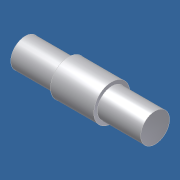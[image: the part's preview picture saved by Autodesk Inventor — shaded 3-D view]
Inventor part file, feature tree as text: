
AUTODESK INVENTOR PART (.ipt)
format: ipt  version: unknown  size: 171,520 bytes
history: native  units: in
note: dims shown in document units (in); Inventor stores cm internally (conversion verified against a paired STEP export)
features: revolve x1, sketch x1
ambient origin geometry x8: Origin, YZ Plane, XZ Plane, XY Plane, X Axis, Y Axis, Z Axis, Center Point
bodies: Solid1 (feature_tree)
feature tree (2):
  revolve  "Revolution1"  [1 undecoded]
  sketch  "Sketch1"  dims[d0=0.375in d1=0.375in d2=0.375in d3=0.125in d4=0.125in d5=0.1562in d6=90.0deg]
note: 1 required parameter value undecoded (feature->parameter linkage not recoverable at this tier; creation-order binding heuristic only, values carry confidence <= 0.55)
